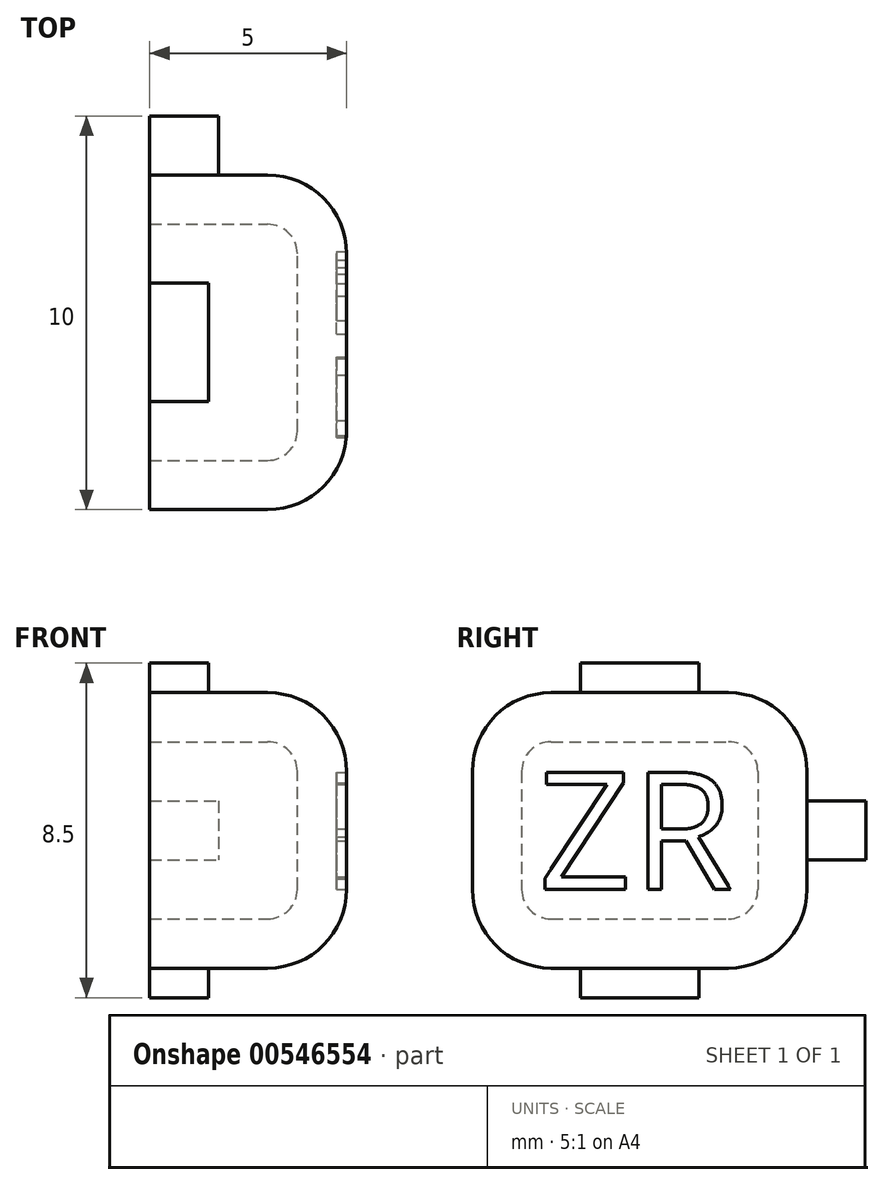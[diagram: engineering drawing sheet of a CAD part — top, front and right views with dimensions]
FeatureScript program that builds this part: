
annotation { "Feature Type Name" : "Feature", "Feature Type Description" : "" }
export const myFeature = defineFeature(function(context is Context, id is Id, definition is map)
    precondition{}
    {
        {
            var Q0;
            Q0=qCreatedBy(makeId("Right.planeOp"),FACE);
            var sketch = newSketch(context, id + "F0", { "sketchPlane" : qUnion([Q0])});
            skLineSegment(sketch, "E0.bottom", {"start": v(-4.25, 3.5) * mm, "end": v(4.25, 3.5) * mm});
            skLineSegment(sketch, "E0.top", {"start": v(-4.25, -3.5) * mm, "end": v(4.25, -3.5) * mm});
            skLineSegment(sketch, "E0.left", {"start": v(-4.25, 3.5) * mm, "end": v(-4.25, -3.5) * mm});
            skLineSegment(sketch, "E0.right", {"start": v(4.25, 3.5) * mm, "end": v(4.25, -3.5) * mm});
            skPoint(sketch, "E0.middle", {"position": v(0, 0) * mm});
            skSolve(sketch);
        }
        {
            var Q0;
            Q0=makeQuery(id+"F0.imprint","IMPRINT",FACE,{"disambiguationData":[TD([[makeQuery(id+"F0.imprint","IMPRINT",EDGE,{"derivedFrom":sQuery(id+"F0.wireOp",EDGE,"E0.bottom")}),-1.0]])]});
            extrude(context, id + "F1", {"entities" : qUnion([Q0]), "endBound" : BoundingType.SYMMETRIC, "depth" : 5 * mm, "offsetDistance" : 25 * mm});
        }
        {
            var Q0;
            Q0=makeQuery(id+"F1.opExtrude","CAP_FACE",FACE,{"disambiguationData":[OSD([sQuery(id+"F0.wireOp",EDGE,"E0.bottom"),sQuery(id+"F0.wireOp",EDGE,"E0.top"),sQuery(id+"F0.wireOp",EDGE,"E0.left"),sQuery(id+"F0.wireOp",EDGE,"E0.right")])],"isStart":false});
            var Q1;
            Q1=makeQuery(id+"F1.opExtrude","SWEPT_EDGE",EDGE,{"disambiguationData":[OSD([sQuery(id+"F0.wireOp",EDGE,"E0.bottom"),sQuery(id+"F0.wireOp",EDGE,"E0.left")])]});
            var Q2;
            Q2=makeQuery(id+"F1.opExtrude","SWEPT_EDGE",EDGE,{"disambiguationData":[OSD([sQuery(id+"F0.wireOp",EDGE,"E0.bottom"),sQuery(id+"F0.wireOp",EDGE,"E0.right")])]});
            var Q3;
            Q3=makeQuery(id+"F1.opExtrude","SWEPT_EDGE",EDGE,{"disambiguationData":[OSD([sQuery(id+"F0.wireOp",EDGE,"E0.top"),sQuery(id+"F0.wireOp",EDGE,"E0.right")])]});
            var Q4;
            Q4=makeQuery(id+"F1.opExtrude","SWEPT_EDGE",EDGE,{"disambiguationData":[OSD([sQuery(id+"F0.wireOp",EDGE,"E0.top"),sQuery(id+"F0.wireOp",EDGE,"E0.left")])]});
            fillet(context, id + "F2", {"entities" : qUnion([Q0, Q1, Q2, Q3, Q4]), "radius" : 2 * mm, "tangentPropagation" : true, "allowEdgeOverflow" : false});
        }
        {
            var Q0;
            Q0=makeQuery(id+"F1.opExtrude","CAP_FACE",FACE,{"disambiguationData":[OSD([sQuery(id+"F0.wireOp",EDGE,"E0.bottom"),sQuery(id+"F0.wireOp",EDGE,"E0.top"),sQuery(id+"F0.wireOp",EDGE,"E0.left"),sQuery(id+"F0.wireOp",EDGE,"E0.right")])],"isStart":true});
            shell(context, id + "F3", {"entities" : qUnion([Q0]), "thickness" : 1.25 * mm});
        }
        {
            var Q0;
            Q0=makeQuery(id+"F1.opExtrude","CAP_FACE",FACE,{"disambiguationData":[OSD([sQuery(id+"F0.wireOp",EDGE,"E0.bottom"),sQuery(id+"F0.wireOp",EDGE,"E0.top"),sQuery(id+"F0.wireOp",EDGE,"E0.left"),sQuery(id+"F0.wireOp",EDGE,"E0.right")])],"isStart":false});
            var sketch = newSketch(context, id + "F4", { "sketchPlane" : qUnion([Q0])});
            skText(sketch, "E1", { "text": "ZR", "fontName": "OpenSans-Regular.ttf"});
            const initialGuessF4  = {"E1": [-0.00258, -0.0015, 1, 0, 0.003]};
            skSetInitialGuess(sketch, initialGuessF4);
            skSolve(sketch);
        }
        {
            var Q0;
            Q0=qSketchRegion(id+"F4",true);
            extrude(context, id + "F5", {"entities" : qUnion([Q0]), "operationType" : NewBodyOperationType.REMOVE, "oppositeDirection" : true, "depth" : .25 * mm, "offsetDistance" : 25 * mm});
        }
        {
            var Q0;
            Q0=makeQuery(id+"F1.opExtrude","CAP_FACE",FACE,{"disambiguationData":[OSD([sQuery(id+"F0.wireOp",EDGE,"E0.bottom"),sQuery(id+"F0.wireOp",EDGE,"E0.top"),sQuery(id+"F0.wireOp",EDGE,"E0.left"),sQuery(id+"F0.wireOp",EDGE,"E0.right")])],"isStart":true});
            var sketch = newSketch(context, id + "F6", { "sketchPlane" : qUnion([Q0])});
            skLineSegment(sketch, "E2.bottom", {"start": v(1.5, 3.5) * mm, "end": v(-1.5, 3.5) * mm});
            skLineSegment(sketch, "E2.top", {"start": v(1.5, 4.25) * mm, "end": v(-1.5, 4.25) * mm});
            skLineSegment(sketch, "E2.left", {"start": v(1.5, 3.5) * mm, "end": v(1.5, 4.25) * mm});
            skLineSegment(sketch, "E2.right", {"start": v(-1.5, 3.5) * mm, "end": v(-1.5, 4.25) * mm});
            skPoint(sketch, "E2.middle", {"position": v(0, 3.87) * mm});
            skLineSegment(sketch, "E3.MirrorCS", {"start": v(-1.5, -3.5) * mm, "end": v(-1.5, -4.25) * mm});
            skLineSegment(sketch, "E4.MirrorCS", {"start": v(1.5, -3.5) * mm, "end": v(1.5, -4.25) * mm});
            skLineSegment(sketch, "E5.MirrorCS", {"start": v(1.5, -3.5) * mm, "end": v(-1.5, -3.5) * mm});
            skLineSegment(sketch, "E6.MirrorCS", {"start": v(1.5, -4.25) * mm, "end": v(-1.5, -4.25) * mm});
            skPoint(sketch, "E7.MirrorP", {"position": v(0, -3.87) * mm});
            skSolve(sketch);
        }
        {
            var Q0;
            Q0=qSketchRegion(id+"F6",true);
            extrude(context, id + "F7", {"entities" : qUnion([Q0]), "operationType" : NewBodyOperationType.ADD, "oppositeDirection" : true, "depth" : 1.5 * mm, "offsetDistance" : 25 * mm});
        }
        {
            var Q0;
            Q0=makeQuery(id+"F1.opExtrude","SWEPT_FACE",FACE,{"disambiguationData":[OSD([sQuery(id+"F0.wireOp",EDGE,"E0.right")])]});
            var sketch = newSketch(context, id + "F8", { "sketchPlane" : qUnion([Q0])});
            skLineSegment(sketch, "E8.bottom", {"start": v(2.5, 0.75) * mm, "end": v(0.75, 0.75) * mm});
            skLineSegment(sketch, "E8.top", {"start": v(2.5, -0.75) * mm, "end": v(0.75, -0.75) * mm});
            skLineSegment(sketch, "E8.left", {"start": v(2.5, 0.75) * mm, "end": v(2.5, -0.75) * mm});
            skLineSegment(sketch, "E8.right", {"start": v(0.75, 0.75) * mm, "end": v(0.75, -0.75) * mm});
            skPoint(sketch, "E8.middle", {"position": v(1.62, 0) * mm});
            skPoint(sketch, "E8.middle.positionSnap0", {"position": v(2.5, 0) * mm});
            skPoint(sketch, "E8.centerSnap0", {"position": v(2.5, 0) * mm});
            skSolve(sketch);
        }
        {
            var Q0;
            Q0=qSketchRegion(id+"F8",true);
            extrude(context, id + "F9", {"entities" : qUnion([Q0]), "operationType" : NewBodyOperationType.ADD, "depth" : 1.5 * mm, "offsetDistance" : 25 * mm});
        }
    });
